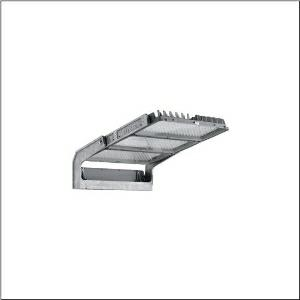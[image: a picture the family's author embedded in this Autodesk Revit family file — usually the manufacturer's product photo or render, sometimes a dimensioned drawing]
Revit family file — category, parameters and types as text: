
# Revit family: floodlight_fl_11_maxi_pro___rs07_5xa779128k01gb_3833
name_source: partatom
category: Lighting Fixtures
units: mm (PartAtom-declared; Revit-internal decimal feet)

## family parameters
Cut with Voids When Loaded = No
Host = Face
Light Source = No
Part Type = Normal
Room Calculation Point = No
Round Connector Dimension = Use Diameter
Shared = No

## types (1)
- --- (1 x LED, 149760 lm, 1285.1 W, 5700K)
    Apparent Load = 1285 VA
    CIE Flux Codes = 80 93 99 100 99
    Color Rendering = 80
    Color Temperature = 5700K
    Default Elevation = 1800 mm
    Description = Floodlight FL 11  maxi  pro floodlight; light control with lens of PMMA; cover panel of toughened safety glass, transparent; light distribution: RS07, rotationally symmetric direct distribution, LEDcolour temperature: 5700K, rated luminous flux: 149.760lm, colour rendering: CRI > 80, light colour: 857; luminous efficacy: 117lm/W; brightness control: DALI 2; with terminal, 5-pole, max. 2.5mm², mains connection: 220..240V/380..400V AC, 50/60Hz, surge voltage resistance: line to ground: 10kV, service life up to 100,000h L90. Typical operating time: 1000h per year, ECG replaceable separately, LED unit replaceable without ESD environment, dustproof LED module, dimming range 10..100%; 1285W floodlight with 3x LED unit of diecast aluminium, coated grey; length: 1.003mm / width: 651mm / height: 338mm; mounting bracket, of diecast aluminium, uncoated, natural, protection rating (complete): IP66; insulation class (complete): insulation class I (protective earthing); certification: CE, ENEC, VDE; ball protection: ball impact resistant, only for outdoor installations in the designated locations, permissible operating ambient temperature: -45..+55°C, permissible storage temperature: -40..+85°Cpackaging unit: 1 piece

Light Distribution: RS07
    Height = 320 mm
    Lamp = 1 x LED
    Lamp Light Flux = 149760 lm
    Lamp Power = 1285.1 W
    Lamp count = 1
    Length = 1002 mm
    Luminous efficacy = 117 lm/W
    Manufacturer = Siteco
    ModVariant = No
    Model = 5XA779128K01GB
    Mounting Place = Ceiling
    Mounting Type = Surface mounted
    Number of Poles = 1
    OnlyDefault = Yes
    Power Factor = 1
    Product Name = Floodlight FL 11 maxi pro | RS07
    Product group = floodlight | ceiling mounted
    ProductGroupID = 301
    Protection Class = Protection class I
    Protection Degree = IP 66
    RLX_Detail_Level = 1
    RLX_Emergency_Light_Flux = 0 lm
    RLX_Emergency_Type = 0
    RLX_Emergency_Type_DB = No
    RlxData = <blob elided: 40253 chars, md5=e7b8db20>
    Socket = socket
    Standby Power = 0 W
    System Light Flux = 149760 lm
    System Power = 1285 W
    Type Comments = factory setting: luminous flux: 100 % | dim-lin: 254 | 875 mA
    Type Image = l_1356210.jpg
    URL = http://relux.com
    VarID = @adj_023710
    Voltage = 0 V
    Weight = 0.00 kg
    Width = 655 mm

## geometry (parser evidence)
native form markers: Blend x4, Sweep x11
no freeform markers — native parametric forms only
